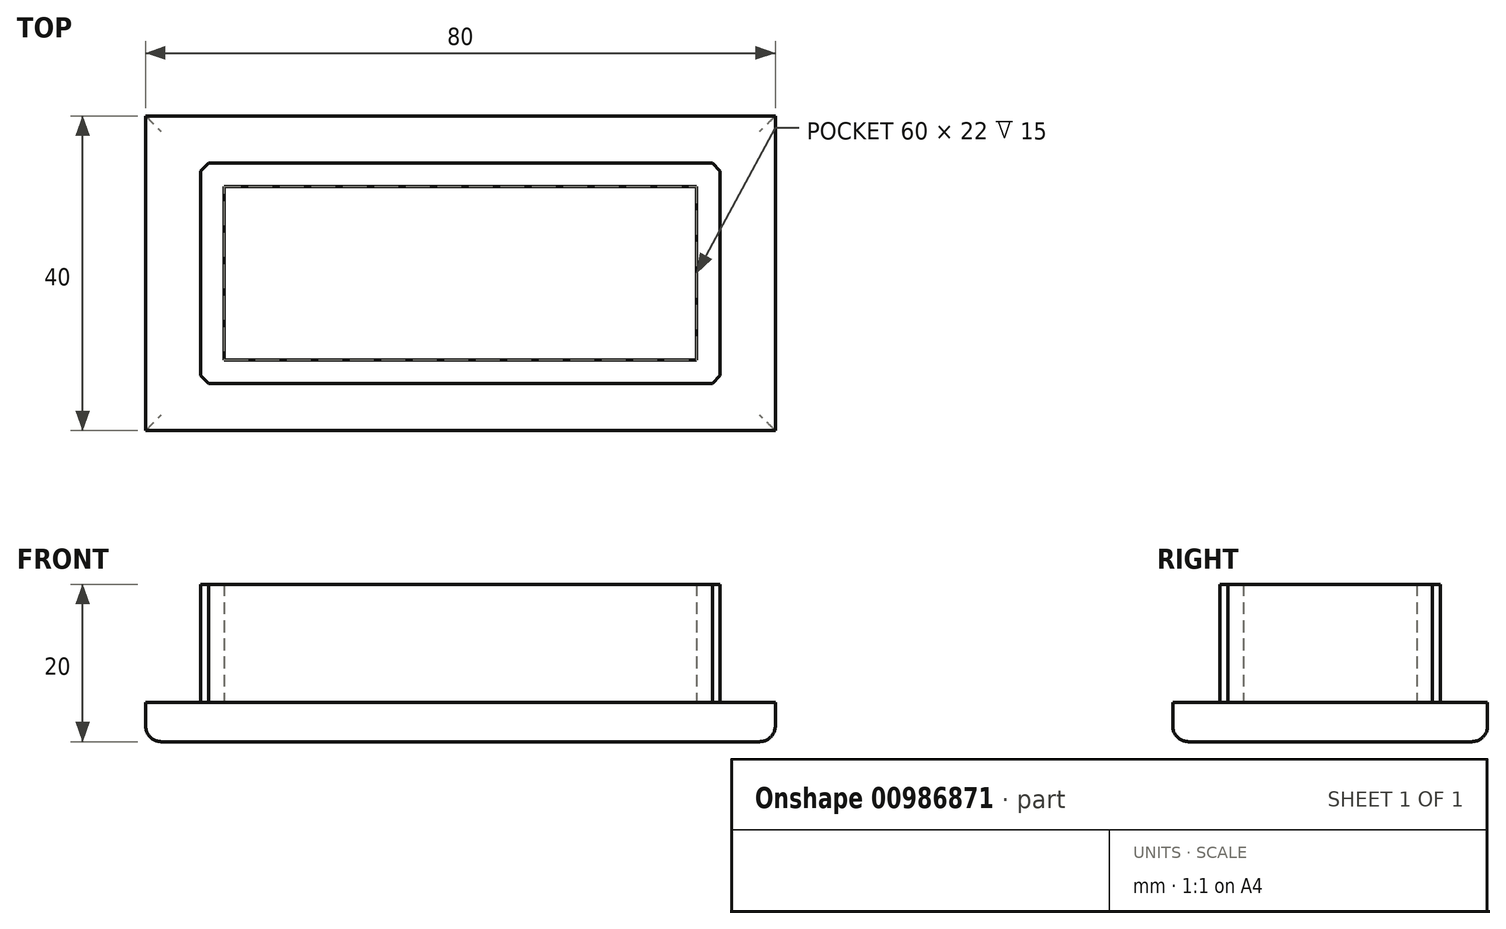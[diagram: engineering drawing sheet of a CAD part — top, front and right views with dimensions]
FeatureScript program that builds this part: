
annotation { "Feature Type Name" : "Feature", "Feature Type Description" : "" }
export const myFeature = defineFeature(function(context is Context, id is Id, definition is map)
    precondition{}
    {
        {
            var Q0;
            Q0=qCreatedBy(makeId("Top.planeOp"),FACE);
            var sketch = newSketch(context, id + "F0", { "sketchPlane" : qUnion([Q0])});
            skLineSegment(sketch, "E0.bottom", {"start": v(40, 20) * mm, "end": v(-40, 20) * mm});
            skLineSegment(sketch, "E0.top", {"start": v(40, -20) * mm, "end": v(-40, -20) * mm});
            skLineSegment(sketch, "E0.left", {"start": v(40, 20) * mm, "end": v(40, -20) * mm});
            skLineSegment(sketch, "E0.right", {"start": v(-40, 20) * mm, "end": v(-40, -20) * mm});
            skPoint(sketch, "E0.middle", {"position": v(0, 0) * mm});
            skSolve(sketch);
        }
        {
            var Q0;
            Q0=makeQuery(id+"F0.imprint","IMPRINT",FACE,{"disambiguationData":[TD([[makeQuery(id+"F0.imprint","IMPRINT",EDGE,{"derivedFrom":sQuery(id+"F0.wireOp",EDGE,"E0.bottom")}),1.0]])]});
            extrude(context, id + "F1", {"entities" : qUnion([Q0]), "depth" : 5 * mm, "offsetDistance" : 25 * mm});
        }
        {
            var Q0;
            Q0=makeQuery(id+"F1.opExtrude","CAP_FACE",FACE,{"disambiguationData":[OSD([sQuery(id+"F0.wireOp",EDGE,"E0.bottom"),sQuery(id+"F0.wireOp",EDGE,"E0.top"),sQuery(id+"F0.wireOp",EDGE,"E0.left"),sQuery(id+"F0.wireOp",EDGE,"E0.right")])],"isStart":false});
            var sketch = newSketch(context, id + "F2", { "sketchPlane" : qUnion([Q0])});
            skLineSegment(sketch, "E1.bottom", {"start": v(33, 14) * mm, "end": v(-33, 14) * mm});
            skLineSegment(sketch, "E1.top", {"start": v(33, -14) * mm, "end": v(-33, -14) * mm});
            skLineSegment(sketch, "E1.left", {"start": v(33, 14) * mm, "end": v(33, -14) * mm});
            skLineSegment(sketch, "E1.right", {"start": v(-33, 14) * mm, "end": v(-33, -14) * mm});
            skPoint(sketch, "E1.middle", {"position": v(0, 0) * mm});
            skLineSegment(sketch, "E2.bottom", {"start": v(30, 11) * mm, "end": v(-30, 11) * mm});
            skLineSegment(sketch, "E2.top", {"start": v(30, -11) * mm, "end": v(-30, -11) * mm});
            skLineSegment(sketch, "E2.left", {"start": v(30, 11) * mm, "end": v(30, -11) * mm});
            skLineSegment(sketch, "E2.right", {"start": v(-30, 11) * mm, "end": v(-30, -11) * mm});
            skSolve(sketch);
        }
        {
            var Q0;
            Q0=makeQuery(id+"F2.imprint","IMPRINT",FACE,{"disambiguationData":[TD([[makeQuery(id+"F2.imprint","IMPRINT",EDGE,{"derivedFrom":sQuery(id+"F2.wireOp",EDGE,"E1.bottom")}),1.0]])]});
            extrude(context, id + "F3", {"entities" : qUnion([Q0]), "operationType" : NewBodyOperationType.ADD, "depth" : 15 * mm, "offsetDistance" : 25 * mm});
        }
        {
            var Q0;
            Q0=makeQuery(id+"F1.opExtrude","CAP_EDGE",EDGE,{"disambiguationData":[OSD([sQuery(id+"F0.wireOp",EDGE,"E0.top")])],"isStart":true});
            var Q1;
            Q1=makeQuery(id+"F1.opExtrude","CAP_EDGE",EDGE,{"disambiguationData":[OSD([sQuery(id+"F0.wireOp",EDGE,"E0.right")])],"isStart":true});
            var Q2;
            Q2=makeQuery(id+"F1.opExtrude","CAP_EDGE",EDGE,{"disambiguationData":[OSD([sQuery(id+"F0.wireOp",EDGE,"E0.bottom")])],"isStart":true});
            var Q3;
            Q3=makeQuery(id+"F1.opExtrude","CAP_EDGE",EDGE,{"disambiguationData":[OSD([sQuery(id+"F0.wireOp",EDGE,"E0.left")])],"isStart":true});
            fillet(context, id + "F4", {"entities" : qUnion([Q0, Q1, Q2, Q3]), "radius" : 2 * mm, "tangentPropagation" : true, "allowEdgeOverflow" : false});
        }
        {
            var Q0;
            Q0=makeQuery(id+"F3.opExtrude","SWEPT_EDGE",EDGE,{"disambiguationData":[OSD([sQuery(id+"F2.wireOp",EDGE,"E1.top"),sQuery(id+"F2.wireOp",EDGE,"E1.right")])]});
            var Q1;
            Q1=makeQuery(id+"F3.opExtrude","SWEPT_EDGE",EDGE,{"disambiguationData":[OSD([sQuery(id+"F2.wireOp",EDGE,"E1.bottom"),sQuery(id+"F2.wireOp",EDGE,"E1.right")])]});
            var Q2;
            Q2=makeQuery(id+"F3.opExtrude","SWEPT_EDGE",EDGE,{"disambiguationData":[OSD([sQuery(id+"F2.wireOp",EDGE,"E1.top"),sQuery(id+"F2.wireOp",EDGE,"E1.left")])]});
            var Q3;
            Q3=makeQuery(id+"F3.opExtrude","SWEPT_EDGE",EDGE,{"disambiguationData":[OSD([sQuery(id+"F2.wireOp",EDGE,"E1.bottom"),sQuery(id+"F2.wireOp",EDGE,"E1.left")])]});
            chamfer(context, id + "F5", {"entities" : qUnion([Q0, Q1, Q2, Q3]), "width" : 1 * mm, "tangentPropagation" : true});
        }
    });
